# Revit family: DHUMAT
name_source: partatom
category: Modelos genéricos
revit_build: Autodesk Revit 2017 (Build: 20160225_1515(x64)
units: mm (PartAtom-declared; Revit-internal decimal feet)

## family parameters
Compartido = No
Corte con vacíos al cargar = No
Cota de conector redondo = Diámetro de uso
Puede alojar armadura = No
Punto de cálculo de habitación = No
Se basa en plano de trabajo = No
Siempre vertical = Sí
Tipo de pieza = Normal

## types (6) — shared parameters
Fabricante = Casals Ventilación
URL = www.casals.com
esp = 2 mm  [stored 0.00656168 ft]

## per-type parameters (varying)
| type | A | B | E | H | L | L1 | L2 | a | b | c |
| DHUMAT 315-355 | 600 mm | 600 mm | 312 mm  [stored 1.02362 ft] | 278 mm  [stored 0.912073 ft] | 496 mm | 181 mm | 313 mm | 200 mm  [stored 0.656168 ft] | 254 mm | 485 mm  [stored 1.59121 ft] |
| DHUMAT 400-450 | 700 mm  [stored 2.29659 ft] | 700 mm  [stored 2.29659 ft] | 344 mm | 278 mm  [stored 0.912073 ft] | 596 mm | 265 mm | 329 mm | 286 mm | 255 mm | 585 mm  [stored 1.91929 ft] |
| DHUMAT 500-560 | 900 mm | 900 mm | 344 mm | 338 mm  [stored 1.10892 ft] | 796 mm | 314 mm | 480 mm | 240 mm  [stored 0.787402 ft] | 508 mm | 785 mm |
| DHUMAT 630 | 1000 mm | 1000 mm | 376 mm  [stored 1.2336 ft] | 338 mm  [stored 1.10892 ft] | 896 mm | 367 mm | 527 mm | 327 mm | 507 mm | 885 mm |
| DHUMAT 710-800 | 1200 mm | 1200 mm | 457 mm | 374 mm  [stored 1.22703 ft] | 1096 mm | 441 mm  [stored 1.44685 ft] | 654 mm | 344 mm | 688 mm | 1085 mm |
| DHUMAT 900-1000 | 1500 mm | 1500 mm | 563 mm  [stored 1.84711 ft] | 441 mm  [stored 1.44685 ft] | 1382 mm | 553 mm  [stored 1.8143 ft] | 827 mm | 461 mm  [stored 1.51247 ft] | 839 mm | 1371 mm |

note: [stored X ft] marks values corroborated as IEEE doubles in the binary element streams (Revit-internal decimal feet)
